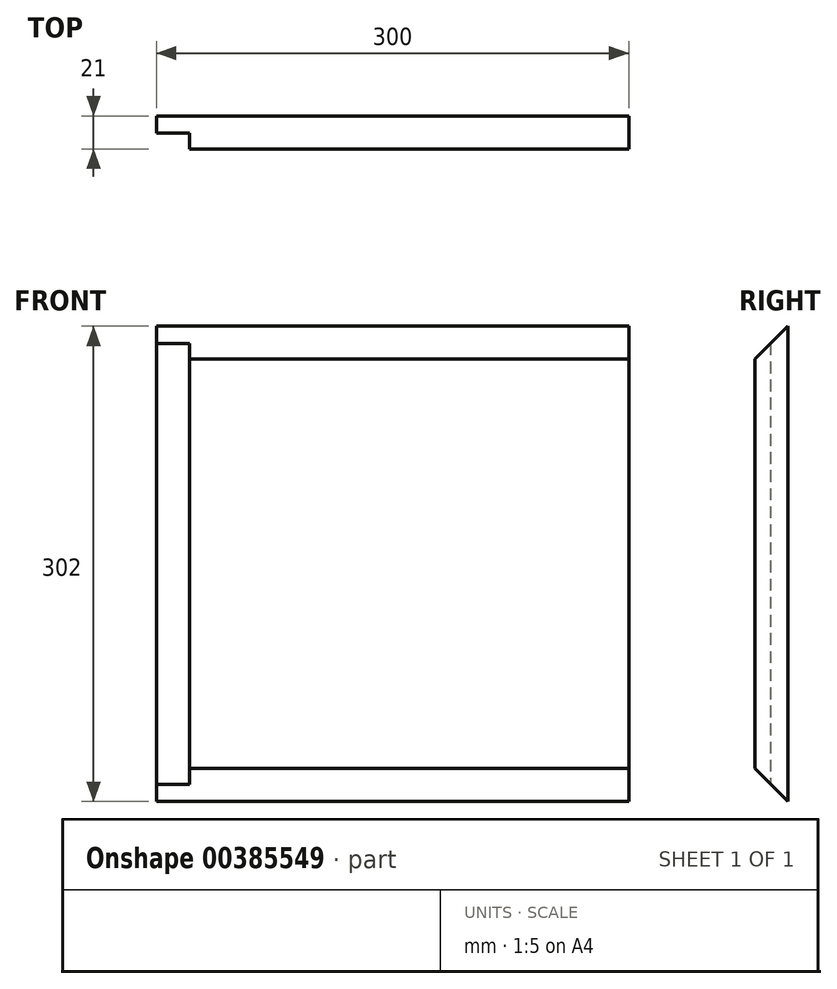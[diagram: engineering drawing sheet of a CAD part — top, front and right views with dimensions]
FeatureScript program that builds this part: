
annotation { "Feature Type Name" : "Feature", "Feature Type Description" : "" }
export const myFeature = defineFeature(function(context is Context, id is Id, definition is map)
    precondition{}
    {
        {
            var Q0;
            Q0=qCreatedBy(makeId("Front.planeOp"),FACE);
            var sketch = newSketch(context, id + "F0", { "sketchPlane" : qUnion([Q0])});
            skLineSegment(sketch, "E0.bottom", {"start": v(150, -151) * mm, "end": v(-150, -151) * mm});
            skLineSegment(sketch, "E0.top", {"start": v(150, 151) * mm, "end": v(-150, 151) * mm});
            skLineSegment(sketch, "E0.left", {"start": v(150, -151) * mm, "end": v(150, 151) * mm});
            skLineSegment(sketch, "E0.right", {"start": v(-150, -151) * mm, "end": v(-150, 151) * mm});
            skPoint(sketch, "E0.middle", {"position": v(0, 0) * mm});
            skSolve(sketch);
        }
        {
            var Q0;
            Q0=makeQuery(id+"F0.imprint","IMPRINT",FACE,{"disambiguationData":[TD([[makeQuery(id+"F0.imprint","IMPRINT",EDGE,{"derivedFrom":sQuery(id+"F0.wireOp",EDGE,"E0.bottom")}),-1.0]])]});
            extrude(context, id + "F1", {"entities" : qUnion([Q0]), "depth" : 21 * mm});
        }
        {
            var Q0;
            Q0=makeQuery(id+"F1.opExtrude","CAP_EDGE",EDGE,{"disambiguationData":[OSD([sQuery(id+"F0.wireOp",EDGE,"E0.top")])],"isStart":false});
            var Q1;
            Q1=makeQuery(id+"F1.opExtrude","CAP_EDGE",EDGE,{"disambiguationData":[OSD([sQuery(id+"F0.wireOp",EDGE,"E0.bottom")])],"isStart":false});
            chamfer(context, id + "F2", {"entities" : qUnion([Q0, Q1]), "width" : 21 * mm, "tangentPropagation" : true});
        }
        {
            var Q0;
            Q0=makeQuery(id+"F1.opExtrude","CAP_FACE",FACE,{"disambiguationData":[OSD([sQuery(id+"F0.wireOp",EDGE,"E0.bottom"),sQuery(id+"F0.wireOp",EDGE,"E0.top"),sQuery(id+"F0.wireOp",EDGE,"E0.left"),sQuery(id+"F0.wireOp",EDGE,"E0.right")])],"isStart":false});
            var sketch = newSketch(context, id + "F3", { "sketchPlane" : qUnion([Q0])});
            skLineSegment(sketch, "E1.bottom", {"start": v(-150, 151) * mm, "end": v(-129, 151) * mm});
            skLineSegment(sketch, "E1.top", {"start": v(-150, -151) * mm, "end": v(-129, -151) * mm});
            skLineSegment(sketch, "E1.left", {"start": v(-150, 151) * mm, "end": v(-150, -151) * mm});
            skLineSegment(sketch, "E1.right", {"start": v(-129, 151) * mm, "end": v(-129, -151) * mm});
            skSolve(sketch);
        }
        {
            var Q0;
            Q0 = qSketchRegion(id + "F3", true);
            extrude(context, id + "F4", {"entities" : qUnion([Q0]), "operationType" : NewBodyOperationType.REMOVE, "oppositeDirection" : true, "depth" : 10 * mm});
        }
    });
